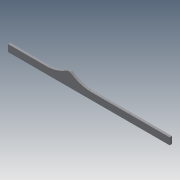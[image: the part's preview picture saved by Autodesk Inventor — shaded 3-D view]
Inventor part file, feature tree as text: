
AUTODESK INVENTOR PART (.ipt)
format: ipt  version: 2013 (Build 170138000, 138)  size: 98,304 bytes
history: native  units: mm
features: extrude x1, sketch x1
ambient origin geometry x8: Origin, YZ Plane, XZ Plane, XY Plane, X Axis, Y Axis, Z Axis, Center Point
bodies: Solid1 (feature_tree)
feature tree (2):
  extrude  "Extrusion1"  Depth=6.0mm
  sketch  "Sketch1"  dims[d0=140.0mm d1=6.0mm d2=35.0mm d3=35.0mm d4=35.0mm d5=0.1mm d6=6.0mm d7=0.1mm d8=6.0mm d9=0.1mm d10=6.0mm d24=2.0mm d25=0.0mm]
